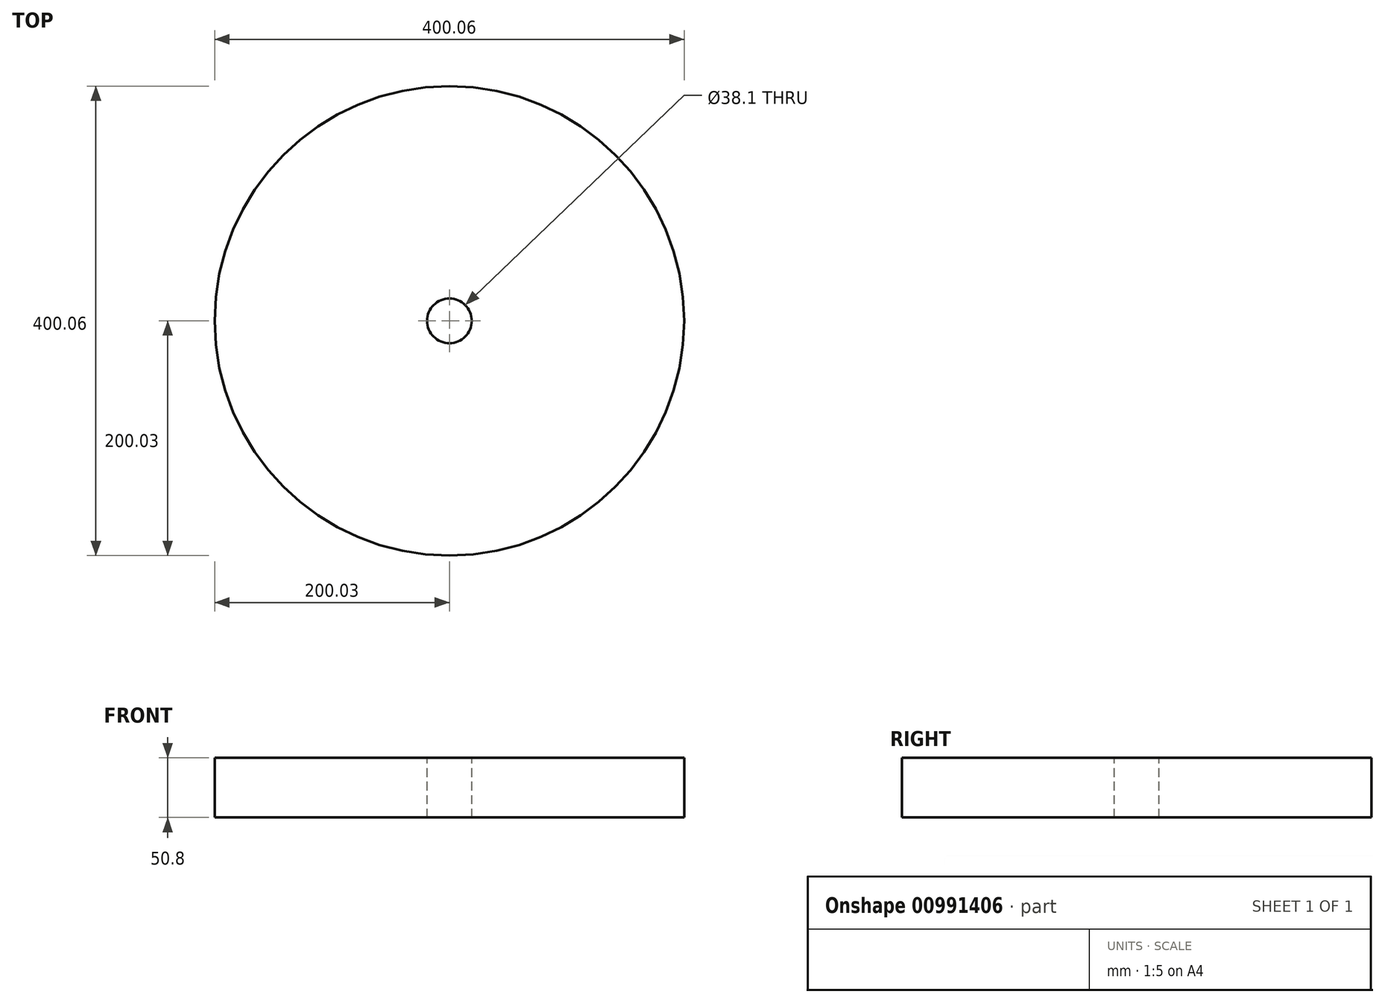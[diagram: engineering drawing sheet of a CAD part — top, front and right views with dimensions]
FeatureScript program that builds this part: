
annotation { "Feature Type Name" : "Feature", "Feature Type Description" : "" }
export const myFeature = defineFeature(function(context is Context, id is Id, definition is map)
    precondition{}
    {
        {
            var Q0;
            Q0=qCreatedBy(makeId("Top.planeOp"),FACE);
            var sketch = newSketch(context, id + "F0", { "sketchPlane" : qUnion([Q0])});
            skCircle(sketch, "E0", {"center": v(0, 0) * mm, "radius": 200.03 * mm});
            skSolve(sketch);
        }
        {
            var Q0;
            Q0 = qSketchRegion(id + "F0", true);
            extrude(context, id + "F1", {"entities" : qUnion([Q0]), "endBound" : BoundingType.SYMMETRIC, "depth" : 50.8 * mm, "offsetDistance" : 25.4 * mm});
        }
        {
            var Q0;
            Q0=makeQuery(id+"F1.opExtrude","CAP_FACE",FACE,{"disambiguationData":[OSD([sQuery(id+"F0.wireOp",EDGE,"E0")])],"isStart":false});
            var sketch = newSketch(context, id + "F2", { "sketchPlane" : qUnion([Q0])});
            skCircle(sketch, "E1", {"center": v(0, 0) * mm, "radius": 19.05 * mm});
            skSolve(sketch);
        }
        {
            var Q0;
            Q0 = qSketchRegion(id + "F2", true);
            extrude(context, id + "F3", {"entities" : qUnion([Q0]), "operationType" : NewBodyOperationType.REMOVE, "endBound" : BoundingType.THROUGH_ALL, "oppositeDirection" : true, "depth" : 25.4 * mm, "offsetDistance" : 25.4 * mm});
        }
    });
